# Revit family: Shower-Slidebar-KOHLER-26313W_1
name_source: partatom
category: Specialty Equipment
revit_build: Autodesk Revit 2017 (Build: 20160225_1515(x64)
units: mm (PartAtom-declared; Revit-internal decimal feet)

## family parameters
Cut with Voids When Loaded = No
Host = Face
OmniClass Number = 23.31.25.00
OmniClass Title = Toilet and Bath Specialties
Part Type = Normal
Room Calculation Point = No
Round Connector Dimension = Use Diameter
Shared = No

## types (5) — shared parameters
ADA Compliant = No
Assembly Code = C1030200
Date Modified = 02/09/2021
Default Elevation = 42"
Description = 100 cm Slidebar
Height = 40 1/16"
Length = 3 9/16"
Manufacturer = KOHLER Co.
Master Format 2014 = 10 28 00
Master Format 2014 Name = Toilet, Bath, and Laundry Accessories
Material = Brass Construction
URL = https://www.kohler.co.uk
WaterSense Certified = No
Width = 6 15/16"

## per-type parameters (varying)
| type | Finish | Model | Type |
| CP-Polished Chrome | Kohler-Metal-CP-Polished_Chrome | 26313W-CP | 4 |
| BN-Roman Silver | Kohler-Metal-BN-Roman_Silver | 26313W-BN | 3 |
| BL-Matte Black | Kohler-Metal-BL-Matte_Black | 26313W-BL | 2 |
| SN-Champagne Gold | Kohler-Metal-SN-Champagne_Gold | 26313W-SN | 5 |
| 2MB-Vibrant Brushed Moderne Brass | Kohler-Metal-2MB-Vibrant_Brushed_Moderne_Brass | 26313W-2MB | 1 |

## geometry (parser evidence)
native form markers: Sweep x4
no freeform markers — native parametric forms only
